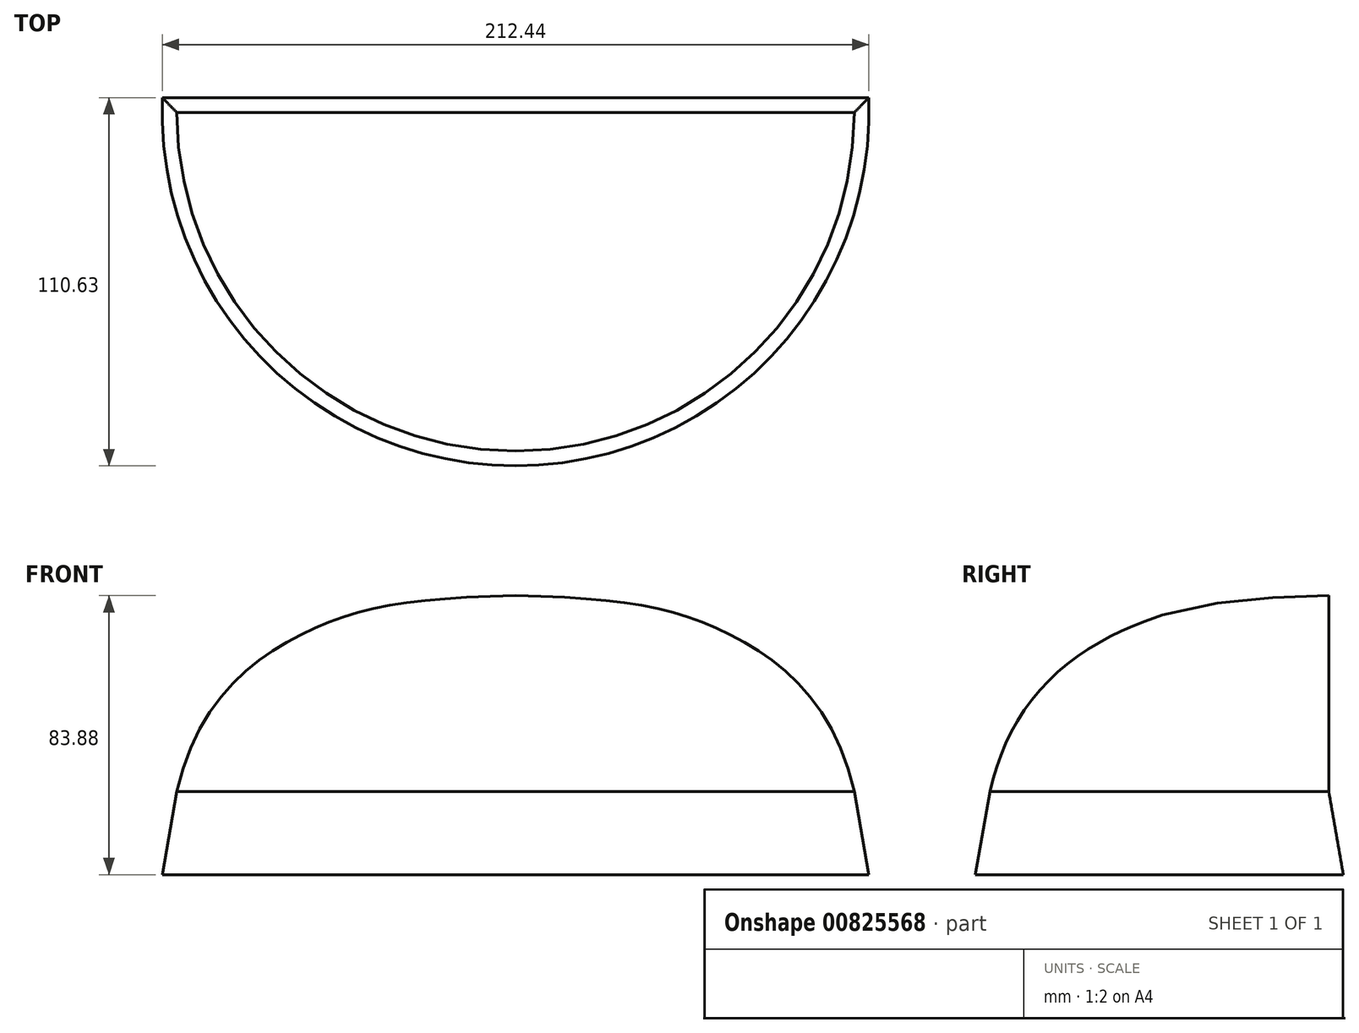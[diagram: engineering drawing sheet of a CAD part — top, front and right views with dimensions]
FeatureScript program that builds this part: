
annotation { "Feature Type Name" : "Feature", "Feature Type Description" : "" }
export const myFeature = defineFeature(function(context is Context, id is Id, definition is map)
    precondition{}
    {
        {
            var Q0;
            Q0=qCreatedBy(makeId("Right.planeOp"),FACE);
            var sketch = newSketch(context, id + "F0", { "sketchPlane" : qUnion([Q0])});
            skFitSpline(sketch, "E0", {"points": [v(0, 142.22) * mm, v(-62.82, 131.31) * mm, v(-101.8, 83.34) * mm], "startDerivative": vector(-183.6, -3.95) * mm, "endDerivative": vector(-37.18, -165.23) * mm});
            skLineSegment(sketch, "E1", {"start": v(-101.8, 83.34) * mm, "end": v(0, 83.34) * mm});
            skLineSegment(sketch, "E2", {"start": v(0, 83.34) * mm, "end": v(0, 142.22) * mm, "construction": true});
            skLineSegment(sketch, "E3", {"start": v(0, 142.22) * mm, "end": v(0, 83.34) * mm});
            skSolve(sketch);
        }
        {
            var Q0;
            Q0=makeQuery(id+"F0.imprint","IMPRINT",FACE,{"disambiguationData":[TD([[makeQuery(id+"F0.imprint","IMPRINT",EDGE,{"derivedFrom":sQuery(id+"F0.wireOp",EDGE,"E0")}),1.0]])]});
            var Q1;
            Q1=sQuery(id+"F0.wireOp",EDGE,"E3");
            revolve(context, id + "F1", {"surfaceOperationType" : NewSurfaceOperationType.NEW, "entities" : qUnion([Q0]), "axis" : qUnion([Q1]), "revolveType" : RevolveType.SYMMETRIC, "angle" : 180 * degree});
        }
        {
            var Q0;
            Q0=makeQuery(id+"F1.opRevolve","SWEPT_FACE",FACE,{"disambiguationData":[OSD([sQuery(id+"F0.wireOp",EDGE,"E1")])]});
            extrude(context, id + "F2", {"entities" : qUnion([Q0]), "operationType" : NewBodyOperationType.ADD, "depth" : 25 * mm, "offsetDistance" : 25 * mm, "hasDraft" : true, "draftAngle" : 10 * degree});
        }
    });
